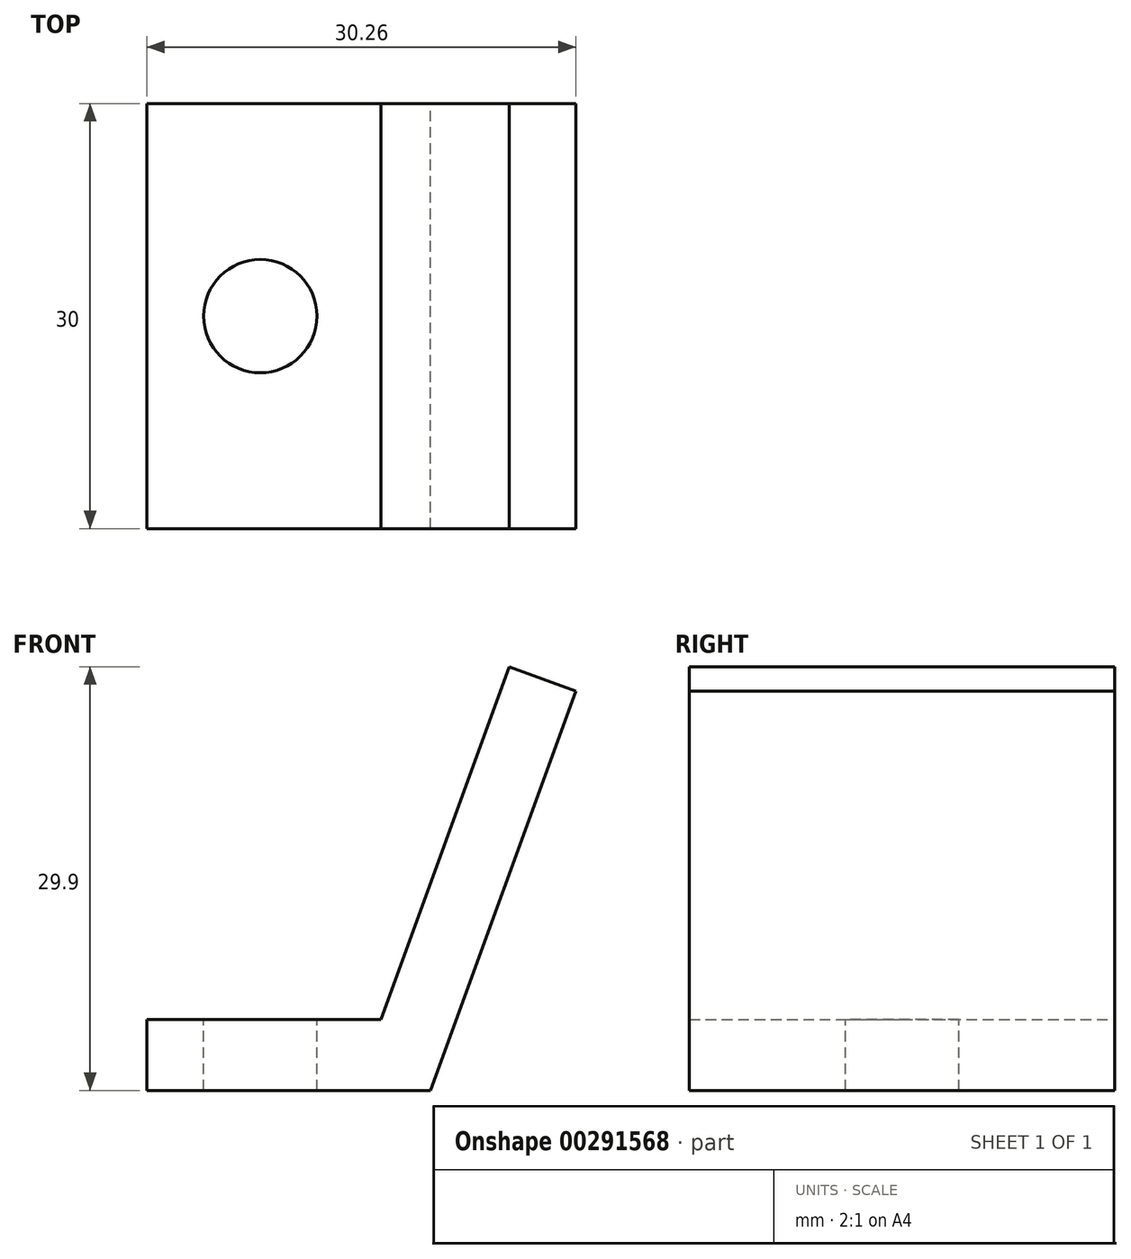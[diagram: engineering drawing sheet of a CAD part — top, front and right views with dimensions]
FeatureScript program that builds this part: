
annotation { "Feature Type Name" : "Feature", "Feature Type Description" : "" }
export const myFeature = defineFeature(function(context is Context, id is Id, definition is map)
    precondition{}
    {
        {
            var Q0;
            Q0=qCreatedBy(makeId("Front.planeOp"),FACE);
            var sketch = newSketch(context, id + "F0", { "sketchPlane" : qUnion([Q0])});
            skLineSegment(sketch, "E0", {"start": v(-50, 0) * mm, "end": v(-50, 5) * mm});
            skLineSegment(sketch, "E1", {"start": v(-50, 5) * mm, "end": v(-33.5, 5) * mm});
            skLineSegment(sketch, "E2", {"start": v(-33.5, 5) * mm, "end": v(-24.44, 29.9) * mm});
            skLineSegment(sketch, "E3", {"start": v(-24.44, 29.9) * mm, "end": v(-19.74, 28.2) * mm});
            skLineSegment(sketch, "E4", {"start": v(-19.74, 28.2) * mm, "end": v(-30, 0) * mm});
            skLineSegment(sketch, "E5", {"start": v(-30, 0) * mm, "end": v(-50, 0) * mm});
            skSolve(sketch);
        }
        {
            var Q0;
            Q0 = qSketchRegion(id + "F0", true);
            extrude(context, id + "F1", {"entities" : qUnion([Q0]), "endBound" : BoundingType.SYMMETRIC, "depth" : 30 * mm});
        }
        {
            var Q0;
            Q0=makeQuery(id+"F1.opExtrude","SWEPT_FACE",FACE,{"disambiguationData":[OSD([sQuery(id+"F0.wireOp",EDGE,"E1")])]});
            var sketch = newSketch(context, id + "F2", { "sketchPlane" : qUnion([Q0])});
            skCircle(sketch, "E6", {"center": v(-42, 0) * mm, "radius": 4 * mm});
            skPoint(sketch, "E7", {"position": v(-50, 0) * mm});
            skSolve(sketch);
        }
        {
            var Q0;
            Q0=makeQuery(id+"F2.imprint","IMPRINT",FACE,{"disambiguationData":[TD([[makeQuery(id+"F2.imprint","IMPRINT",EDGE,{"derivedFrom":sQuery(id+"F2.wireOp",EDGE,"E6")}),1.0]])]});
            extrude(context, id + "F3", {"entities" : qUnion([Q0]), "operationType" : NewBodyOperationType.REMOVE, "oppositeDirection" : true, "depth" : 25 * mm});
        }
    });
